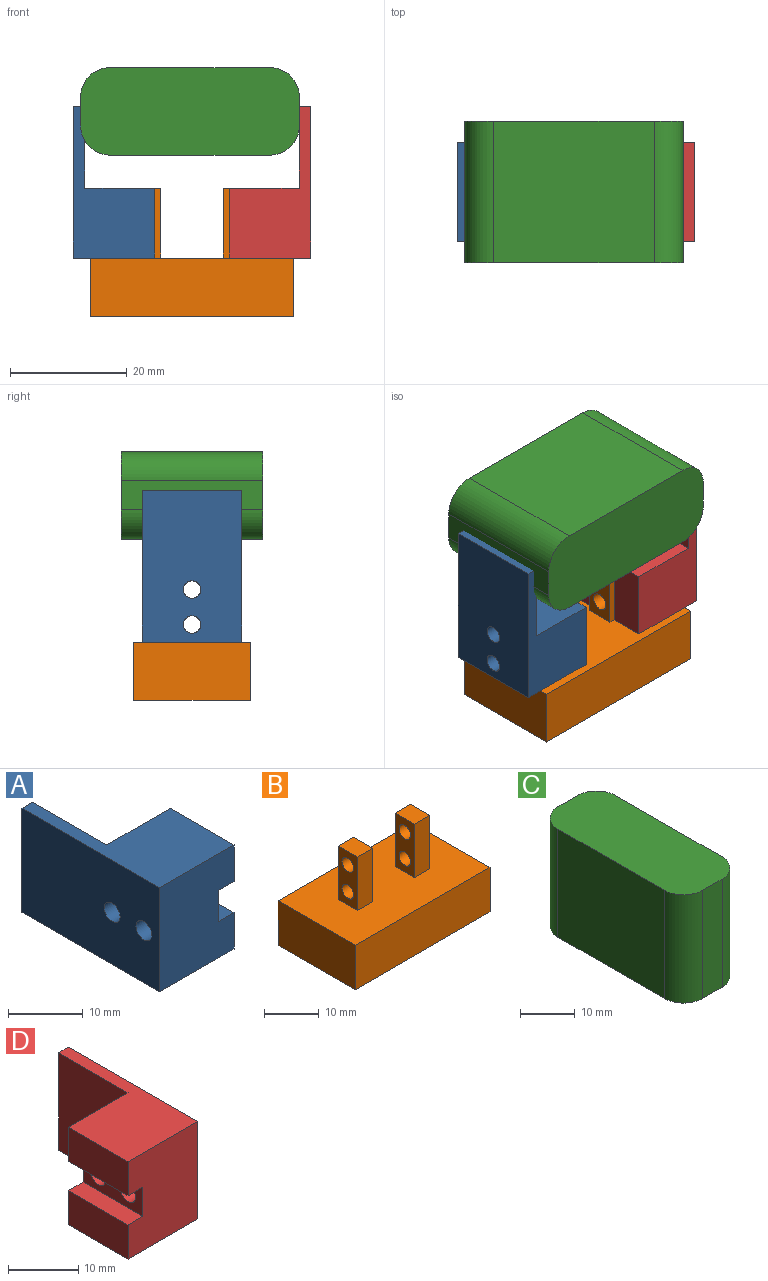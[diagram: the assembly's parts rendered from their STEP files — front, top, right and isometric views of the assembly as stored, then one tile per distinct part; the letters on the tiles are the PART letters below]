
ASSEMBLY  parts=4 mates=2
PART A: 14 faces, bbox 14x26x17 mm
  f0: plane 12x3mm, normal (0,0,-1), area 36mm2, adj f3,f5,f7,f12
  f1: cylinder r=1.5mm len=11mm, axis (1,0,0), area 103.7mm2, adj f3,f13
  f2: cylinder r=1.5mm len=11mm, axis (1,0,0), area 103.7mm2, adj f3,f13
  f3: plane 12x5.1mm, normal (1,0,0), area 47.1mm2, adj f0,f1,f2,f4,f7,f12
  f4: plane 12x3mm, normal (0,0,1), area 36mm2, adj f3,f6,f7,f12
  f5: plane 12x5.95mm, normal (1,0,0), area 71.4mm2, adj f0,f7,f11,f12
  f6: plane 12x5.95mm, normal (1,0,0), area 71.4mm2, adj f4,f7,f10,f12
  f7: plane 17x12mm, normal (0,1,0), area 188.7mm2, adj f0,f3,f4,f5,f6,f8,f10,f11
  f8: plane 17x14mm, normal (1,0,0), area 238mm2, adj f7,f9,f10,f11
  f9: plane 17x2mm, normal (0,1,0), area 34mm2, adj f8,f10,f11,f13
  f10: plane 26x14mm, normal (0,0,-1), area 196mm2, adj f6,f7,f8,f9,f12,f13
  f11: plane 26x14mm, normal (0,0,1), area 196mm2, adj f5,f7,f8,f9,f12,f13
  f12: plane 17x14mm, normal (0,-1,0), area 222.7mm2, adj f0,f3,f4,f5,f6,f10,f11,f13
  f13: plane 26x17mm, normal (-1,0,0), area 427.9mm2, adj f1,f2,f9,f10,f11,f12
PART B: 20 faces, bbox 35x20x22 mm
  f0: plane 35x20mm, normal (0,0,1), area 660mm2, adj f1,f2,f3,f4,f6,f7,f8,f9
  f1: plane 35x10mm, normal (0,1,0), area 350mm2, adj f0,f2,f4,f5
  f2: plane 20x10mm, normal (-1,0,0), area 200mm2, adj f0,f1,f3,f5
  f3: plane 35x10mm, normal (0,-1,0), area 350mm2, adj f0,f2,f4,f5
  f4: plane 20x10mm, normal (1,0,0), area 200mm2, adj f0,f1,f3,f5
  f5: plane 35x20mm, normal (0,0,-1), area 700mm2, adj f1,f2,f3,f4
  f6: plane 12x5mm, normal (-1,0,0), area 45.9mm2, adj f0,f7,f9,f10,f18,f19
  f7: plane 12x4mm, normal (0,-1,0), area 48mm2, adj f0,f6,f8,f10
  f8: plane 12x5mm, normal (1,0,0), area 45.9mm2, adj f0,f7,f9,f10,f18,f19
  f9: plane 12x4mm, normal (0,1,0), area 48mm2, adj f0,f6,f8,f10
  f10: plane 5x4mm, normal (0,0,1), area 20mm2, adj f6,f7,f8,f9
  f11: plane 12x5mm, normal (1,0,0), area 45.9mm2, adj f0,f12,f14,f15,f16,f17
  f12: plane 12x4mm, normal (0,1,0), area 48mm2, adj f0,f11,f13,f15
  f13: plane 12x5mm, normal (-1,0,0), area 45.9mm2, adj f0,f12,f14,f15,f16,f17
  f14: plane 12x4mm, normal (0,-1,0), area 48mm2, adj f0,f11,f13,f15
  f15: plane 5x4mm, normal (0,0,1), area 20mm2, adj f11,f12,f13,f14
  f16: cylinder r=1.5mm len=4mm, axis (1,0,0), area 37.7mm2, adj f11,f13
  f17: cylinder r=1.5mm len=4mm, axis (1,0,0), area 37.7mm2, adj f11,f13
  f18: cylinder r=1.5mm len=4mm, axis (1,0,0), area 37.7mm2, adj f6,f8
  f19: cylinder r=1.5mm len=4mm, axis (1,0,0), area 37.7mm2, adj f6,f8
PART C: 10 faces, bbox 15x37.5x24.3 mm
  f0: plane 27.5x24.25mm, normal (-1,0,0), area 666.9mm2, adj f4,f5,f6,f9
  f1: plane 24.25x5mm, normal (0,-1,0), area 121.3mm2, adj f4,f5,f6,f7
  f2: plane 27.5x24.25mm, normal (1,0,0), area 666.9mm2, adj f4,f5,f7,f8
  f3: plane 24.25x5mm, normal (0,1,0), area 121.3mm2, adj f4,f5,f8,f9
  f4: plane 37.5x15mm, normal (0,0,1), area 541mm2, adj f0,f1,f2,f3,f6,f7,f8,f9
  f5: plane 37.5x15mm, normal (0,0,-1), area 541mm2, adj f0,f1,f2,f3,f6,f7,f8,f9
  f6: cylinder r=5mm len=24.25mm, axis (0,0,1), area 190.5mm2, adj f0,f1,f4,f5
  f7: cylinder r=5mm len=24.25mm, axis (0,0,-1), area 190.5mm2, adj f1,f2,f4,f5
  f8: cylinder r=5mm len=24.25mm, axis (0,0,1), area 190.5mm2, adj f2,f3,f4,f5
  f9: cylinder r=5mm len=24.25mm, axis (0,0,-1), area 190.5mm2, adj f0,f3,f4,f5
PART D: 14 faces, bbox 14x26x17 mm
  f0: cylinder r=1.5mm len=11mm, axis (1,0,0), area 103.7mm2, adj f11,f13
  f1: cylinder r=1.5mm len=11mm, axis (1,0,0), area 103.7mm2, adj f11,f13
  f2: plane 17x14mm, normal (0,-1,0), area 222.7mm2, adj f3,f4,f6,f7,f9,f10,f11,f13
  f3: plane 26x14mm, normal (0,0,1), area 196mm2, adj f2,f5,f6,f8,f12,f13
  f4: plane 26x14mm, normal (0,0,-1), area 196mm2, adj f2,f5,f7,f8,f12,f13
  f5: plane 17x2mm, normal (0,1,0), area 34mm2, adj f3,f4,f12,f13
  f6: plane 12x5.95mm, normal (-1,0,0), area 71.4mm2, adj f2,f3,f8,f9
  f7: plane 12x5.95mm, normal (-1,0,0), area 71.4mm2, adj f2,f4,f8,f10
  f8: plane 17x12mm, normal (0,1,0), area 188.7mm2, adj f3,f4,f6,f7,f9,f10,f11,f12
  f9: plane 12x3mm, normal (0,0,-1), area 36mm2, adj f2,f6,f8,f11
  f10: plane 12x3mm, normal (0,0,1), area 36mm2, adj f2,f7,f8,f11
  f11: plane 12x5.1mm, normal (-1,0,0), area 47.1mm2, adj f0,f1,f2,f8,f9,f10
  f12: plane 17x14mm, normal (-1,0,0), area 238mm2, adj f3,f4,f5,f8
  f13: plane 26x17mm, normal (1,0,0), area 427.9mm2, adj f0,f1,f2,f3,f4,f5
PLACE A rot(axis=(1,0,0),90deg) t=(-20.4,8.5,10)mm
PLACE B t=(0,0,10)mm fixed
PLACE C rot(axis=(0.58,-0.58,0.58),120deg) t=(18.4,12.13,-11.76)mm
PLACE D rot(axis=(1,0,0),90deg) t=(20.4,8.5,10)mm
MATE cylindrical A.f2 <-> B.f16  axis (1,0,0) through (-9.4,0,13)mm
MATE planar D.f12 <-> C.f1  axis (-1,0,0) through (18.4,0,29)mm
